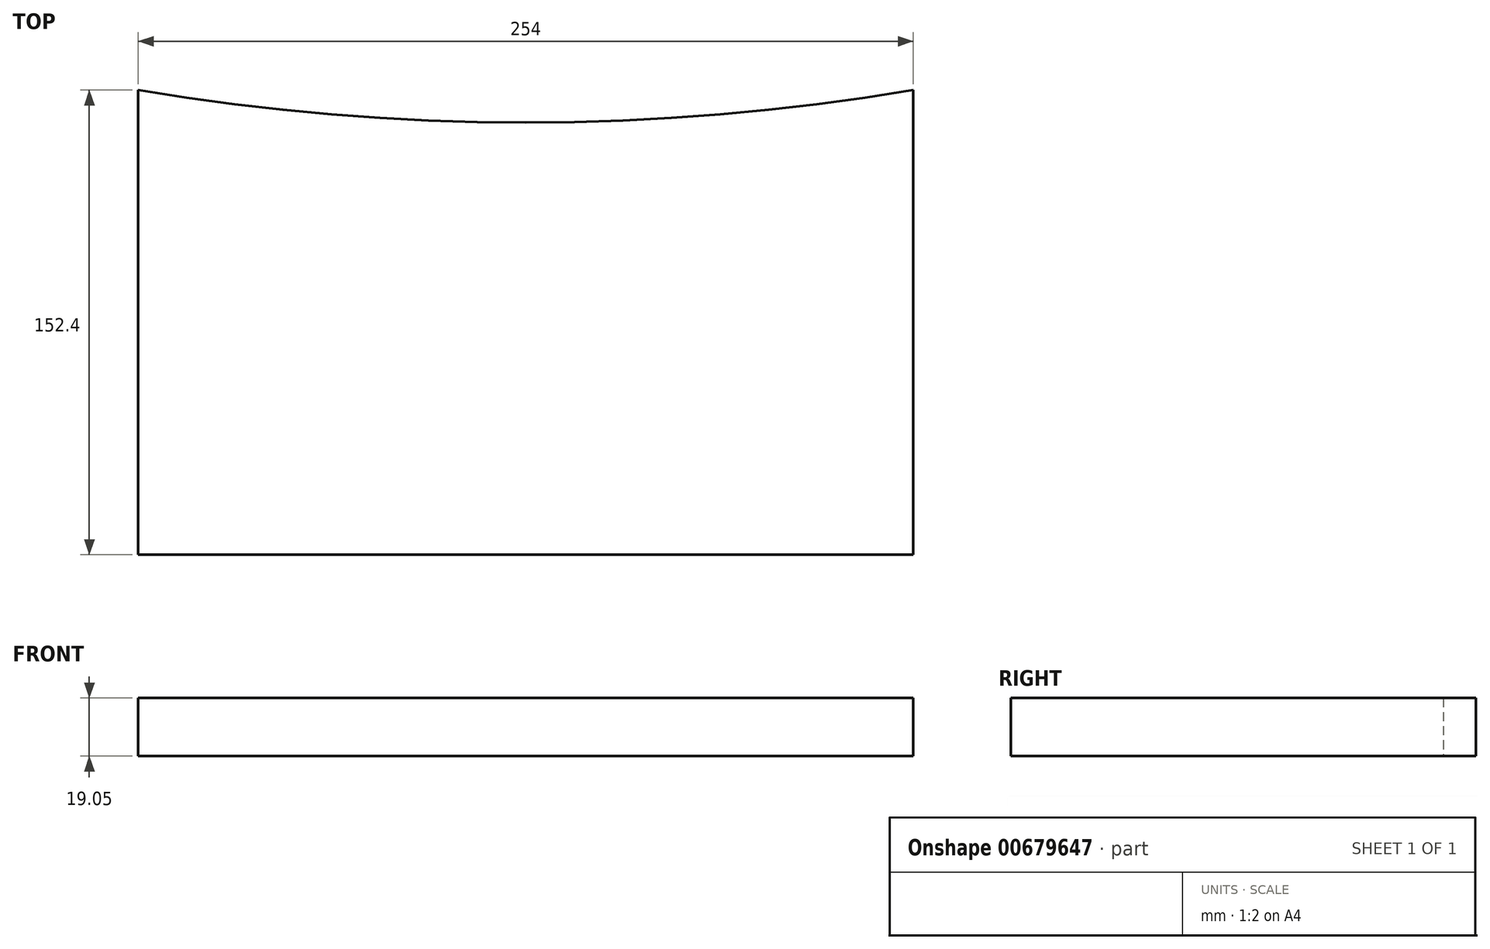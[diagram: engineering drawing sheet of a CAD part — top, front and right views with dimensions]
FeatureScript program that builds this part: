
annotation { "Feature Type Name" : "Feature", "Feature Type Description" : "" }
export const myFeature = defineFeature(function(context is Context, id is Id, definition is map)
    precondition{}
    {
        {
            var Q0;
            Q0=qCreatedBy(makeId("Top.planeOp"),FACE);
            var sketch = newSketch(context, id + "F0", { "sketchPlane" : qUnion([Q0])});
            skArc(sketch, "E0", {"start": v(-127, -751.34) * mm, "mid": v(0, -762) * mm, "end": v(127, -751.34) * mm});
            skLineSegment(sketch, "E1", {"start": v(0, 0) * mm, "end": v(0, -762) * mm, "construction": true});
            skLineSegment(sketch, "E2", {"start": v(127, -903.74) * mm, "end": v(-127, -903.74) * mm});
            skPoint(sketch, "E3", {"position": v(0, -762) * mm});
            skPoint(sketch, "E4.orphan", {"position": v(0, -1524) * mm});
            skLineSegment(sketch, "E5", {"start": v(-127, -903.74) * mm, "end": v(-127, -751.34) * mm});
            skLineSegment(sketch, "E6", {"start": v(127, -903.74) * mm, "end": v(127, -751.34) * mm});
            skSolve(sketch);
        }
        {
            var Q0;
            Q0 = qSketchRegion(id + "F0", true);
            extrude(context, id + "F1", {"entities" : qUnion([Q0]), "depth" : 19.05 * mm, "offsetDistance" : 25.4 * mm});
        }
    });
